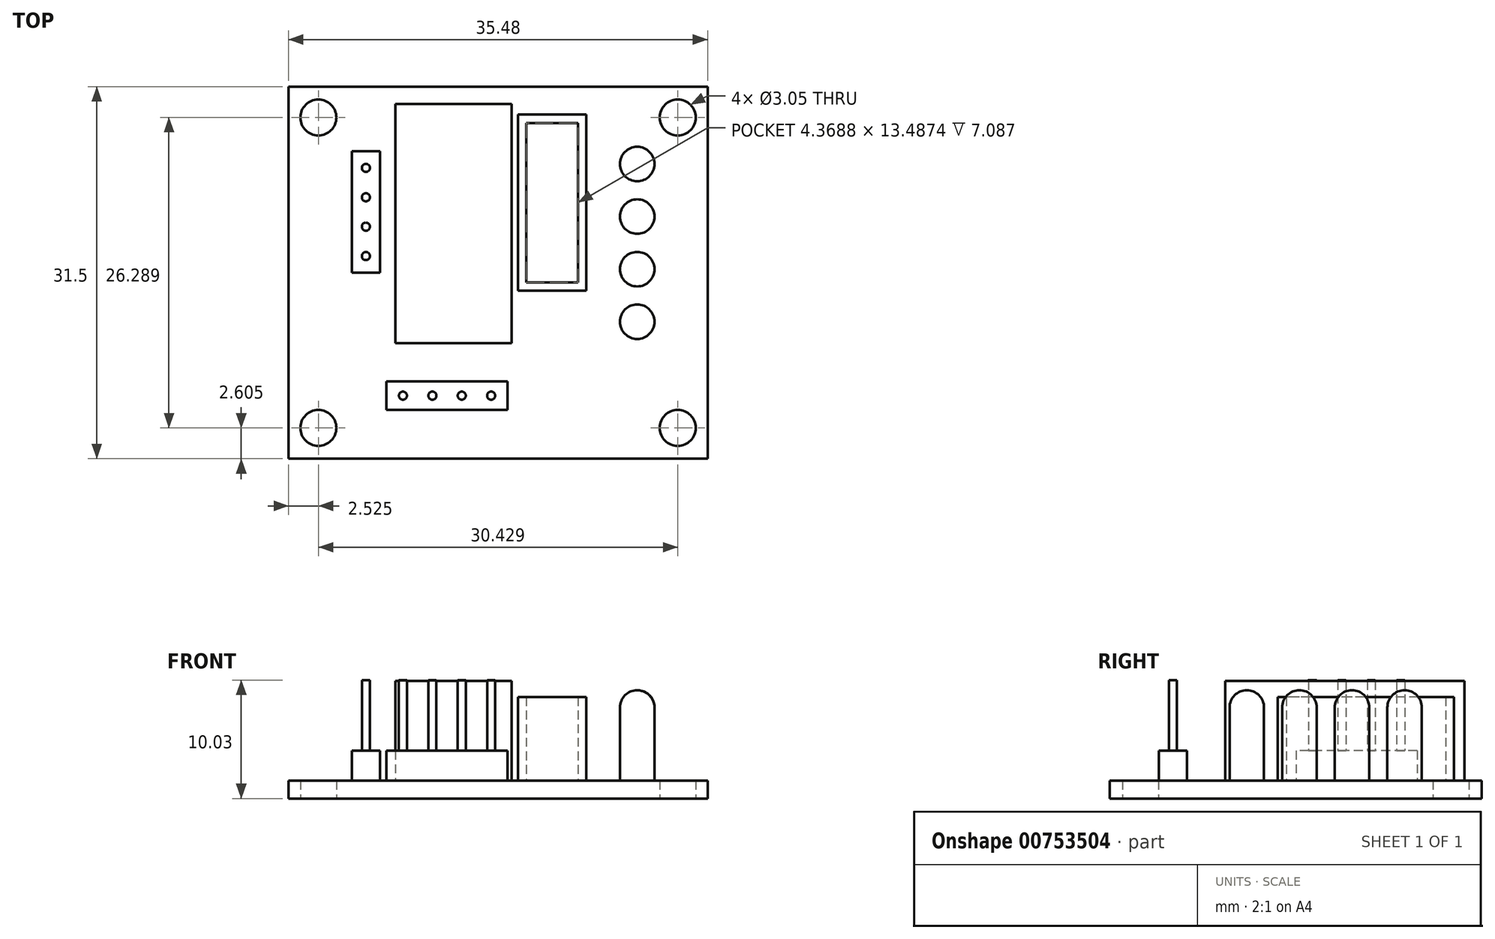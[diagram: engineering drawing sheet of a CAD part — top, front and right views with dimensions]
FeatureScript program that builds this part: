
annotation { "Feature Type Name" : "Feature", "Feature Type Description" : "" }
export const myFeature = defineFeature(function(context is Context, id is Id, definition is map)
    precondition{}
    {
        {
            var Q0;
            Q0=qCreatedBy(makeId("Top.planeOp"),FACE);
            var sketch = newSketch(context, id + "F0", { "sketchPlane" : qUnion([Q0])});
            skLineSegment(sketch, "E0.bottom", {"start": v(-17.74, 15.75) * mm, "end": v(17.74, 15.75) * mm});
            skLineSegment(sketch, "E0.top", {"start": v(-17.74, -15.75) * mm, "end": v(17.74, -15.75) * mm});
            skLineSegment(sketch, "E0.left", {"start": v(-17.74, 15.75) * mm, "end": v(-17.74, -15.75) * mm});
            skLineSegment(sketch, "E0.right", {"start": v(17.74, 15.75) * mm, "end": v(17.74, -15.75) * mm});
            skLineSegment(sketch, "E1.bottom", {"start": v(-15.21, 13.14) * mm, "end": v(15.21, 13.14) * mm, "construction": true});
            skLineSegment(sketch, "E1.top", {"start": v(-15.21, -13.14) * mm, "end": v(15.21, -13.14) * mm, "construction": true});
            skLineSegment(sketch, "E1.left", {"start": v(-15.21, 13.14) * mm, "end": v(-15.21, -13.14) * mm, "construction": true});
            skLineSegment(sketch, "E1.right", {"start": v(15.21, 13.14) * mm, "end": v(15.21, -13.14) * mm, "construction": true});
            skCircle(sketch, "E2", {"center": v(-15.21, 13.14) * mm, "radius": 1.52 * mm});
            skCircle(sketch, "E3", {"center": v(-15.21, -13.14) * mm, "radius": 1.52 * mm});
            skCircle(sketch, "E4", {"center": v(15.21, -13.14) * mm, "radius": 1.52 * mm});
            skCircle(sketch, "E5", {"center": v(15.21, 13.14) * mm, "radius": 1.52 * mm});
            skSolve(sketch);
        }
        {
            var Q0;
            Q0=makeQuery(id+"F0.imprint","IMPRINT",FACE,{"disambiguationData":[TD([[makeQuery(id+"F0.imprint","IMPRINT",EDGE,{"derivedFrom":sQuery(id+"F0.wireOp",EDGE,"E0.bottom")}),-1.0]])]});
            extrude(context, id + "F1", {"entities" : qUnion([Q0]), "depth" : 1.5 * mm, "offsetDistance" : 25.4 * mm});
        }
        {
            var Q0;
            Q0=makeQuery(id+"F1.opExtrude","CAP_FACE",FACE,{"disambiguationData":[OSD([sQuery(id+"F0.wireOp",EDGE,"E0.bottom"),sQuery(id+"F0.wireOp",EDGE,"E0.top"),sQuery(id+"F0.wireOp",EDGE,"E0.left"),sQuery(id+"F0.wireOp",EDGE,"E0.right"),sQuery(id+"F0.wireOp",EDGE,"E2"),sQuery(id+"F0.wireOp",EDGE,"E3"),sQuery(id+"F0.wireOp",EDGE,"E4"),sQuery(id+"F0.wireOp",EDGE,"E5")])],"isStart":false});
            var sketch = newSketch(context, id + "F2", { "sketchPlane" : qUnion([Q0])});
            skLineSegment(sketch, "E6", {"start": v(11.79, 9.2) * mm, "end": v(11.79, 4.75) * mm, "construction": true});
            skLineSegment(sketch, "E7", {"start": v(11.79, 4.75) * mm, "end": v(11.79, 0.3) * mm, "construction": true});
            skLineSegment(sketch, "E8", {"start": v(11.79, 0.3) * mm, "end": v(11.79, -4.15) * mm, "construction": true});
            skCircle(sketch, "E9", {"center": v(11.79, -4.15) * mm, "radius": 1.46 * mm});
            skCircle(sketch, "E10", {"center": v(11.79, 0.3) * mm, "radius": 1.46 * mm});
            skCircle(sketch, "E11", {"center": v(11.79, 4.75) * mm, "radius": 1.46 * mm});
            skCircle(sketch, "E12", {"center": v(11.79, 9.2) * mm, "radius": 1.46 * mm});
            skLineSegment(sketch, "E13.bottom", {"start": v(1.69, 13.39) * mm, "end": v(7.48, 13.39) * mm});
            skLineSegment(sketch, "E13.top", {"start": v(1.69, -1.52) * mm, "end": v(7.48, -1.52) * mm});
            skLineSegment(sketch, "E13.left", {"start": v(1.69, 13.39) * mm, "end": v(1.69, -1.52) * mm});
            skLineSegment(sketch, "E13.right", {"start": v(7.48, 13.39) * mm, "end": v(7.48, -1.52) * mm});
            skLineSegment(sketch, "E14.bottom", {"start": v(2.4, 12.67) * mm, "end": v(6.77, 12.67) * mm});
            skLineSegment(sketch, "E14.top", {"start": v(2.4, -0.81) * mm, "end": v(6.77, -0.81) * mm});
            skLineSegment(sketch, "E14.left", {"start": v(2.4, 12.67) * mm, "end": v(2.4, -0.81) * mm});
            skLineSegment(sketch, "E14.right", {"start": v(6.77, 12.67) * mm, "end": v(6.77, -0.81) * mm});
            skLineSegment(sketch, "E15", {"start": v(1.69, 5.93) * mm, "end": v(2.4, 5.93) * mm, "construction": true});
            skLineSegment(sketch, "E16", {"start": v(4.58, -1.52) * mm, "end": v(4.58, -0.81) * mm, "construction": true});
            skLineSegment(sketch, "E17", {"start": v(7.48, 5.93) * mm, "end": v(6.77, 5.93) * mm, "construction": true});
            skLineSegment(sketch, "E18", {"start": v(4.58, 13.39) * mm, "end": v(4.58, 12.67) * mm, "construction": true});
            skLineSegment(sketch, "E19.bottom", {"start": v(-8.7, 14.27) * mm, "end": v(1.16, 14.27) * mm});
            skLineSegment(sketch, "E19.top", {"start": v(-8.7, -5.97) * mm, "end": v(1.16, -5.97) * mm});
            skLineSegment(sketch, "E19.left", {"start": v(-8.7, 14.27) * mm, "end": v(-8.7, -5.97) * mm});
            skLineSegment(sketch, "E19.right", {"start": v(1.16, 14.27) * mm, "end": v(1.16, -5.97) * mm});
            skLineSegment(sketch, "E20", {"start": v(-11.19, 8.88) * mm, "end": v(-11.19, 6.39) * mm, "construction": true});
            skLineSegment(sketch, "E21", {"start": v(-11.19, 6.39) * mm, "end": v(-11.19, 3.9) * mm, "construction": true});
            skLineSegment(sketch, "E22", {"start": v(-11.19, 3.9) * mm, "end": v(-11.19, 1.4) * mm, "construction": true});
            skCircle(sketch, "E23", {"center": v(-11.19, 1.4) * mm, "radius": 0.34 * mm});
            skCircle(sketch, "E24", {"center": v(-11.19, 3.9) * mm, "radius": 0.34 * mm});
            skCircle(sketch, "E25", {"center": v(-11.19, 6.39) * mm, "radius": 0.34 * mm});
            skCircle(sketch, "E26", {"center": v(-11.19, 8.88) * mm, "radius": 0.34 * mm});
            skLineSegment(sketch, "E27", {"start": v(-8.05, -10.41) * mm, "end": v(-5.56, -10.41) * mm, "construction": true});
            skLineSegment(sketch, "E28", {"start": v(-5.56, -10.41) * mm, "end": v(-3.07, -10.41) * mm, "construction": true});
            skLineSegment(sketch, "E29", {"start": v(-3.07, -10.41) * mm, "end": v(-0.58, -10.41) * mm, "construction": true});
            skCircle(sketch, "E30", {"center": v(-8.05, -10.41) * mm, "radius": 0.34 * mm});
            skCircle(sketch, "E31", {"center": v(-5.56, -10.41) * mm, "radius": 0.34 * mm});
            skCircle(sketch, "E32", {"center": v(-3.07, -10.41) * mm, "radius": 0.34 * mm});
            skCircle(sketch, "E33", {"center": v(-0.58, -10.41) * mm, "radius": 0.34 * mm});
            skLineSegment(sketch, "E34.bottom", {"start": v(-12.38, 10.27) * mm, "end": v(-10, 10.27) * mm});
            skLineSegment(sketch, "E34.top", {"start": v(-12.38, 0.01) * mm, "end": v(-10, 0.01) * mm});
            skLineSegment(sketch, "E34.left", {"start": v(-12.38, 10.27) * mm, "end": v(-12.38, 0.01) * mm});
            skLineSegment(sketch, "E34.right", {"start": v(-10, 10.27) * mm, "end": v(-10, 0.01) * mm});
            skLineSegment(sketch, "E35.bottom", {"start": v(-9.45, -9.22) * mm, "end": v(0.81, -9.22) * mm});
            skLineSegment(sketch, "E35.top", {"start": v(-9.45, -11.6) * mm, "end": v(0.81, -11.6) * mm});
            skLineSegment(sketch, "E35.left", {"start": v(-9.45, -9.22) * mm, "end": v(-9.45, -11.6) * mm});
            skLineSegment(sketch, "E35.right", {"start": v(0.81, -9.22) * mm, "end": v(0.81, -11.6) * mm});
            skLineSegment(sketch, "E36", {"start": v(-4.32, -10.41) * mm, "end": v(-4.32, -9.22) * mm, "construction": true});
            skLineSegment(sketch, "E37", {"start": v(-11.19, 5.14) * mm, "end": v(-12.38, 5.14) * mm, "construction": true});
            skSolve(sketch);
        }
        {
            var Q0;
            Q0=makeQuery(id+"F2.imprint","IMPRINT",FACE,{"disambiguationData":[TD([[makeQuery(id+"F2.imprint","IMPRINT",EDGE,{"derivedFrom":sQuery(id+"F2.wireOp",EDGE,"E19.bottom")}),-1.0]])]});
            extrude(context, id + "F3", {"entities" : qUnion([Q0]), "operationType" : NewBodyOperationType.ADD, "depth" : 8.46 * mm, "offsetDistance" : 25.4 * mm});
        }
        {
            var Q0;
            Q0=makeQuery(id+"F2.imprint","IMPRINT",FACE,{"disambiguationData":[TD([[makeQuery(id+"F2.imprint","IMPRINT",EDGE,{"derivedFrom":sQuery(id+"F2.wireOp",EDGE,"E13.bottom")}),-1.0]])]});
            extrude(context, id + "F4", {"entities" : qUnion([Q0]), "operationType" : NewBodyOperationType.ADD, "depth" : 7.1 * mm, "offsetDistance" : 25.4 * mm});
        }
        {
            var Q0;
            Q0=makeQuery(id+"F2.imprint","IMPRINT",FACE,{"disambiguationData":[TD([[makeQuery(id+"F2.imprint","IMPRINT",EDGE,{"derivedFrom":sQuery(id+"F2.wireOp",EDGE,"E9")}),1.0]])]});
            var Q1;
            Q1=makeQuery(id+"F2.imprint","IMPRINT",FACE,{"disambiguationData":[TD([[makeQuery(id+"F2.imprint","IMPRINT",EDGE,{"derivedFrom":sQuery(id+"F2.wireOp",EDGE,"E10")}),1.0]])]});
            var Q2;
            Q2=makeQuery(id+"F2.imprint","IMPRINT",FACE,{"disambiguationData":[TD([[makeQuery(id+"F2.imprint","IMPRINT",EDGE,{"derivedFrom":sQuery(id+"F2.wireOp",EDGE,"E11")}),1.0]])]});
            var Q3;
            Q3=makeQuery(id+"F2.imprint","IMPRINT",FACE,{"disambiguationData":[TD([[makeQuery(id+"F2.imprint","IMPRINT",EDGE,{"derivedFrom":sQuery(id+"F2.wireOp",EDGE,"E12")}),1.0]])]});
            extrude(context, id + "F5", {"entities" : qUnion([Q0, Q1, Q2, Q3]), "operationType" : NewBodyOperationType.ADD, "depth" : 7.67 * mm, "offsetDistance" : 25.4 * mm});
        }
        {
            var Q0;
            Q0=makeQuery(id+"F5.opExtrude","CAP_EDGE",EDGE,{"disambiguationData":[OSD([sQuery(id+"F2.wireOp",EDGE,"E9")])],"isStart":false});
            var Q1;
            Q1=makeQuery(id+"F5.opExtrude","CAP_EDGE",EDGE,{"disambiguationData":[OSD([sQuery(id+"F2.wireOp",EDGE,"E10")])],"isStart":false});
            var Q2;
            Q2=makeQuery(id+"F5.opExtrude","CAP_EDGE",EDGE,{"disambiguationData":[OSD([sQuery(id+"F2.wireOp",EDGE,"E11")])],"isStart":false});
            var Q3;
            Q3=makeQuery(id+"F5.opExtrude","CAP_EDGE",EDGE,{"disambiguationData":[OSD([sQuery(id+"F2.wireOp",EDGE,"E12")])],"isStart":false});
            fillet(context, id + "F6", {"entities" : qUnion([Q0, Q1, Q2, Q3]), "radius" : 1.46 * mm, "tangentPropagation" : true, "allowEdgeOverflow" : false});
        }
        {
            var Q0;
            Q0=makeQuery(id+"F2.imprint","IMPRINT",FACE,{"disambiguationData":[TD([[makeQuery(id+"F2.imprint","IMPRINT",EDGE,{"derivedFrom":sQuery(id+"F2.wireOp",EDGE,"E23")}),1.0]])]});
            var Q1;
            Q1=makeQuery(id+"F2.imprint","IMPRINT",FACE,{"disambiguationData":[TD([[makeQuery(id+"F2.imprint","IMPRINT",EDGE,{"derivedFrom":sQuery(id+"F2.wireOp",EDGE,"E24")}),1.0]])]});
            var Q2;
            Q2=makeQuery(id+"F2.imprint","IMPRINT",FACE,{"disambiguationData":[TD([[makeQuery(id+"F2.imprint","IMPRINT",EDGE,{"derivedFrom":sQuery(id+"F2.wireOp",EDGE,"E25")}),1.0]])]});
            var Q3;
            Q3=makeQuery(id+"F2.imprint","IMPRINT",FACE,{"disambiguationData":[TD([[makeQuery(id+"F2.imprint","IMPRINT",EDGE,{"derivedFrom":sQuery(id+"F2.wireOp",EDGE,"E26")}),1.0]])]});
            extrude(context, id + "F7", {"entities" : qUnion([Q0, Q1, Q2, Q3]), "operationType" : NewBodyOperationType.ADD, "depth" : 8.53 * mm, "offsetDistance" : 25.4 * mm});
        }
        {
            var Q0;
            Q0=makeQuery(id+"F2.imprint","IMPRINT",FACE,{"disambiguationData":[TD([[makeQuery(id+"F2.imprint","IMPRINT",EDGE,{"derivedFrom":sQuery(id+"F2.wireOp",EDGE,"E30")}),1.0]])]});
            var Q1;
            Q1=makeQuery(id+"F2.imprint","IMPRINT",FACE,{"disambiguationData":[TD([[makeQuery(id+"F2.imprint","IMPRINT",EDGE,{"derivedFrom":sQuery(id+"F2.wireOp",EDGE,"E31")}),1.0]])]});
            var Q2;
            Q2=makeQuery(id+"F2.imprint","IMPRINT",FACE,{"disambiguationData":[TD([[makeQuery(id+"F2.imprint","IMPRINT",EDGE,{"derivedFrom":sQuery(id+"F2.wireOp",EDGE,"E32")}),1.0]])]});
            var Q3;
            Q3=makeQuery(id+"F2.imprint","IMPRINT",FACE,{"disambiguationData":[TD([[makeQuery(id+"F2.imprint","IMPRINT",EDGE,{"derivedFrom":sQuery(id+"F2.wireOp",EDGE,"E33")}),1.0]])]});
            extrude(context, id + "F8", {"entities" : qUnion([Q0, Q1, Q2, Q3]), "operationType" : NewBodyOperationType.ADD, "depth" : 8.53 * mm, "offsetDistance" : 25.4 * mm});
        }
        {
            var Q0;
            Q0=makeQuery(id+"F2.imprint","IMPRINT",FACE,{"disambiguationData":[TD([[makeQuery(id+"F2.imprint","IMPRINT",EDGE,{"derivedFrom":sQuery(id+"F2.wireOp",EDGE,"E23")}),-1.0]])]});
            extrude(context, id + "F9", {"entities" : qUnion([Q0]), "operationType" : NewBodyOperationType.ADD, "depth" : 2.54 * mm, "offsetDistance" : 25.4 * mm});
        }
        {
            var Q0;
            Q0=makeQuery(id+"F2.imprint","IMPRINT",FACE,{"disambiguationData":[TD([[makeQuery(id+"F2.imprint","IMPRINT",EDGE,{"derivedFrom":sQuery(id+"F2.wireOp",EDGE,"E30")}),-1.0]])]});
            extrude(context, id + "F10", {"entities" : qUnion([Q0]), "operationType" : NewBodyOperationType.ADD, "depth" : 2.54 * mm, "offsetDistance" : 25.4 * mm});
        }
    });
